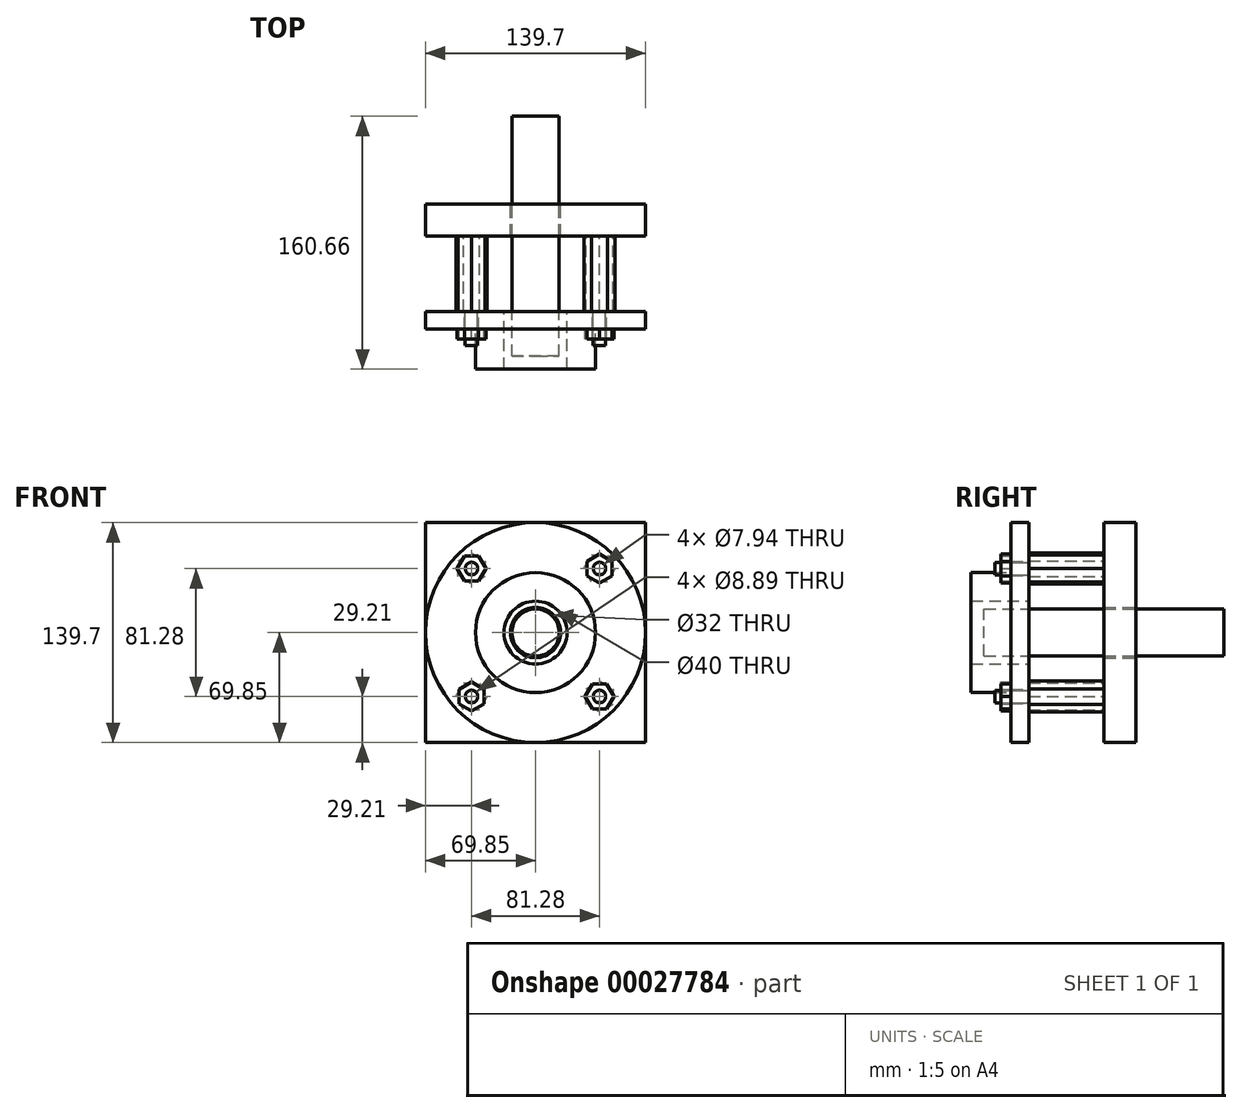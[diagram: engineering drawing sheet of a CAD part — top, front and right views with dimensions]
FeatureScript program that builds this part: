
annotation { "Feature Type Name" : "Feature", "Feature Type Description" : "" }
export const myFeature = defineFeature(function(context is Context, id is Id, definition is map)
    precondition{}
    {
        {
            var Q0;
            Q0=qCreatedBy(makeId("Front.planeOp"),FACE);
            var sketch = newSketch(context, id + "F0", { "sketchPlane" : qUnion([Q0])});
            skCircle(sketch, "E0", {"center": v(0, 0) * mm, "radius": 16 * mm});
            skLineSegment(sketch, "E1.bottom", {"start": v(-69.85, 69.85) * mm, "end": v(69.85, 69.85) * mm});
            skLineSegment(sketch, "E1.top", {"start": v(-69.85, -69.85) * mm, "end": v(69.85, -69.85) * mm});
            skLineSegment(sketch, "E1.left", {"start": v(-69.85, 69.85) * mm, "end": v(-69.85, -69.85) * mm});
            skLineSegment(sketch, "E1.right", {"start": v(69.85, 69.85) * mm, "end": v(69.85, -69.85) * mm});
            skSolve(sketch);
        }
        {
            var Q0;
            Q0=makeQuery(id+"F0.imprint","IMPRINT",FACE,{"disambiguationData":[TD([[makeQuery(id+"F0.imprint","IMPRINT",EDGE,{"derivedFrom":sQuery(id+"F0.wireOp",EDGE,"E0")}),-1.0]])]});
            extrude(context, id + "F1", {"entities" : qUnion([Q0]), "depth" : 20.32 * mm});
        }
        {
            var Q0;
            Q0=makeQuery(id+"F1.opExtrude","CAP_FACE",FACE,{"disambiguationData":[OSD([sQuery(id+"F0.wireOp",EDGE,"E0"),sQuery(id+"F0.wireOp",EDGE,"E1.bottom"),sQuery(id+"F0.wireOp",EDGE,"E1.top"),sQuery(id+"F0.wireOp",EDGE,"E1.left"),sQuery(id+"F0.wireOp",EDGE,"E1.right")])],"isStart":false});
            var sketch = newSketch(context, id + "F2", { "sketchPlane" : qUnion([Q0])});
            skLineSegment(sketch, "E2.bottom", {"start": v(-40.64, -40.64) * mm, "end": v(40.64, -40.64) * mm, "construction": true});
            skLineSegment(sketch, "E2.top", {"start": v(-40.64, 40.64) * mm, "end": v(40.64, 40.64) * mm, "construction": true});
            skLineSegment(sketch, "E2.left", {"start": v(-40.64, -40.64) * mm, "end": v(-40.64, 40.64) * mm, "construction": true});
            skLineSegment(sketch, "E2.right", {"start": v(40.64, -40.64) * mm, "end": v(40.64, 40.64) * mm, "construction": true});
            skLineSegment(sketch, "E3", {"start": v(35.7, 49.21) * mm, "end": v(45.59, 49.21) * mm});
            skLineSegment(sketch, "E4", {"start": v(45.59, 49.21) * mm, "end": v(50.54, 40.64) * mm});
            skLineSegment(sketch, "E5", {"start": v(50.54, 40.64) * mm, "end": v(45.59, 32.07) * mm});
            skLineSegment(sketch, "E6", {"start": v(45.59, 32.07) * mm, "end": v(35.7, 32.07) * mm});
            skLineSegment(sketch, "E7", {"start": v(35.7, 32.07) * mm, "end": v(30.74, 40.64) * mm});
            skLineSegment(sketch, "E8", {"start": v(30.74, 40.64) * mm, "end": v(35.7, 49.21) * mm});
            skLineSegment(sketch, "E9.1.0", {"start": v(-49.21, 35.7) * mm, "end": v(-49.21, 45.59) * mm});
            skLineSegment(sketch, "E9.1.1", {"start": v(-40.64, 30.74) * mm, "end": v(-49.21, 35.7) * mm});
            skLineSegment(sketch, "E9.1.2", {"start": v(-32.07, 35.7) * mm, "end": v(-40.64, 30.74) * mm});
            skLineSegment(sketch, "E9.1.3", {"start": v(-32.07, 45.59) * mm, "end": v(-32.07, 35.7) * mm});
            skLineSegment(sketch, "E9.1.4", {"start": v(-40.64, 50.54) * mm, "end": v(-32.07, 45.59) * mm});
            skLineSegment(sketch, "E9.1.5", {"start": v(-49.21, 45.59) * mm, "end": v(-40.64, 50.54) * mm});
            skLineSegment(sketch, "E9.2.0", {"start": v(-35.7, -49.21) * mm, "end": v(-45.59, -49.21) * mm});
            skLineSegment(sketch, "E9.2.1", {"start": v(-30.74, -40.64) * mm, "end": v(-35.7, -49.21) * mm});
            skLineSegment(sketch, "E9.2.2", {"start": v(-35.7, -32.07) * mm, "end": v(-30.74, -40.64) * mm});
            skLineSegment(sketch, "E9.2.3", {"start": v(-45.59, -32.07) * mm, "end": v(-35.7, -32.07) * mm});
            skLineSegment(sketch, "E9.2.4", {"start": v(-50.54, -40.64) * mm, "end": v(-45.59, -32.07) * mm});
            skLineSegment(sketch, "E9.2.5", {"start": v(-45.59, -49.21) * mm, "end": v(-50.54, -40.64) * mm});
            skPoint(sketch, "E9.center", {"position": v(0, 0) * mm});
            skLineSegment(sketch, "E10.1.3.0", {"start": v(49.21, -35.7) * mm, "end": v(49.21, -45.59) * mm});
            skLineSegment(sketch, "E10.3.3.0", {"start": v(40.64, -30.74) * mm, "end": v(49.21, -35.7) * mm});
            skLineSegment(sketch, "E10.6.3.0", {"start": v(32.07, -35.7) * mm, "end": v(40.64, -30.74) * mm});
            skLineSegment(sketch, "E10.9.3.0", {"start": v(32.07, -45.59) * mm, "end": v(32.07, -35.7) * mm});
            skLineSegment(sketch, "E10.12.3.0", {"start": v(40.64, -50.54) * mm, "end": v(32.07, -45.59) * mm});
            skLineSegment(sketch, "E10.15.3.0", {"start": v(49.21, -45.59) * mm, "end": v(40.64, -50.54) * mm});
            skSolve(sketch);
        }
        {
            var Q0;
            Q0=makeQuery(id+"F2.imprint","IMPRINT",FACE,{"disambiguationData":[TD([[makeQuery(id+"F2.imprint","IMPRINT",EDGE,{"derivedFrom":sQuery(id+"F2.wireOp",EDGE,"E9.1.0")}),-1.0]])]});
            var Q1;
            Q1=makeQuery(id+"F2.imprint","IMPRINT",FACE,{"disambiguationData":[TD([[makeQuery(id+"F2.imprint","IMPRINT",EDGE,{"derivedFrom":sQuery(id+"F2.wireOp",EDGE,"E3")}),-1.0]])]});
            var Q2;
            Q2=makeQuery(id+"F2.imprint","IMPRINT",FACE,{"disambiguationData":[TD([[makeQuery(id+"F2.imprint","IMPRINT",EDGE,{"derivedFrom":sQuery(id+"F2.wireOp",EDGE,"E9.3.0")}),-1.0]])]});
            var Q3;
            Q3=makeQuery(id+"F2.imprint","IMPRINT",FACE,{"disambiguationData":[TD([[makeQuery(id+"F2.imprint","IMPRINT",EDGE,{"derivedFrom":sQuery(id+"F2.wireOp",EDGE,"E9.2.0")}),-1.0]])]});
            var Q4;
            Q4=makeQuery(id+"F2.imprint","IMPRINT",FACE,{"disambiguationData":[TD([[makeQuery(id+"F2.imprint","IMPRINT",EDGE,{"derivedFrom":sQuery(id+"F2.wireOp",EDGE,"E10.1.3.0")}),-1.0]])]});
            extrude(context, id + "F3", {"entities" : qUnion([Q0, Q1, Q2, Q3, Q4]), "operationType" : NewBodyOperationType.ADD, "depth" : 47.88 * mm});
        }
        {
            var Q0;
            Q0=makeQuery(id+"F3.opExtrude","CAP_FACE",FACE,{"disambiguationData":[OSD([sQuery(id+"F2.wireOp",EDGE,"E9.1.0"),sQuery(id+"F2.wireOp",EDGE,"E9.1.1"),sQuery(id+"F2.wireOp",EDGE,"E9.1.2"),sQuery(id+"F2.wireOp",EDGE,"E9.1.3"),sQuery(id+"F2.wireOp",EDGE,"E9.1.4"),sQuery(id+"F2.wireOp",EDGE,"E9.1.5")])],"isStart":false});
            var sketch = newSketch(context, id + "F4", { "sketchPlane" : qUnion([Q0])});
            skLineSegment(sketch, "E11", {"start": v(-40.64, 50.54) * mm, "end": v(-40.64, 30.74) * mm, "construction": true});
            skLineSegment(sketch, "E12", {"start": v(-32.07, 45.59) * mm, "end": v(-49.21, 35.7) * mm, "construction": true});
            skCircle(sketch, "E13", {"center": v(-40.64, 40.64) * mm, "radius": 3.97 * mm});
            skCircle(sketch, "E14.1.0", {"center": v(-40.64, -40.64) * mm, "radius": 3.97 * mm});
            skCircle(sketch, "E14.2.0", {"center": v(40.64, -40.64) * mm, "radius": 3.97 * mm});
            skCircle(sketch, "E14.3.0", {"center": v(40.64, 40.64) * mm, "radius": 3.97 * mm});
            skPoint(sketch, "E14.center", {"position": v(0, 0) * mm});
            skSolve(sketch);
        }
        {
            var Q0;
            Q0=makeQuery(id+"F4.imprint","IMPRINT",FACE,{"disambiguationData":[TD([[makeQuery(id+"F4.imprint","IMPRINT",EDGE,{"derivedFrom":sQuery(id+"F4.wireOp",EDGE,"E13")}),1.0]])]});
            var Q1;
            Q1=makeQuery(id+"F4.imprint","IMPRINT",FACE,{"disambiguationData":[TD([[makeQuery(id+"F4.imprint","IMPRINT",EDGE,{"derivedFrom":sQuery(id+"F4.wireOp",EDGE,"E14.3.0")}),1.0]])]});
            var Q2;
            Q2=makeQuery(id+"F4.imprint","IMPRINT",FACE,{"disambiguationData":[TD([[makeQuery(id+"F4.imprint","IMPRINT",EDGE,{"derivedFrom":sQuery(id+"F4.wireOp",EDGE,"E14.2.0")}),1.0]])]});
            var Q3;
            Q3=makeQuery(id+"F4.imprint","IMPRINT",FACE,{"disambiguationData":[TD([[makeQuery(id+"F4.imprint","IMPRINT",EDGE,{"derivedFrom":sQuery(id+"F4.wireOp",EDGE,"E14.1.0")}),1.0]])]});
            extrude(context, id + "F5", {"entities" : qUnion([Q0, Q1, Q2, Q3]), "operationType" : NewBodyOperationType.ADD, "depth" : 21.59 * mm});
        }
        {
            var Q0;
            Q0=makeQuery(id+"F1.opExtrude","CAP_FACE",FACE,{"disambiguationData":[OSD([sQuery(id+"F0.wireOp",EDGE,"E0"),sQuery(id+"F0.wireOp",EDGE,"E1.bottom"),sQuery(id+"F0.wireOp",EDGE,"E1.top"),sQuery(id+"F0.wireOp",EDGE,"E1.left"),sQuery(id+"F0.wireOp",EDGE,"E1.right")])],"isStart":false});
            var sketch = newSketch(context, id + "F6", { "sketchPlane" : qUnion([Q0])});
            skCircle(sketch, "E15", {"center": v(0, 0) * mm, "radius": 15 * mm});
            skSolve(sketch);
        }
        {
            var Q0;
            Q0=makeQuery(id+"F6.imprint","IMPRINT",FACE,{"disambiguationData":[TD([[makeQuery(id+"F6.imprint","IMPRINT",EDGE,{"derivedFrom":sQuery(id+"F6.wireOp",EDGE,"E15")}),1.0]])]});
            extrude(context, id + "F7", {"entities" : qUnion([Q0]), "endBound" : BoundingType.SYMMETRIC, "depth" : 152.4 * mm});
        }
        {
            var Q0;
            Q0=makeQuery(id+"F3.opExtrude","CAP_FACE",FACE,{"disambiguationData":[OSD([sQuery(id+"F2.wireOp",EDGE,"E9.1.0"),sQuery(id+"F2.wireOp",EDGE,"E9.1.1"),sQuery(id+"F2.wireOp",EDGE,"E9.1.2"),sQuery(id+"F2.wireOp",EDGE,"E9.1.3"),sQuery(id+"F2.wireOp",EDGE,"E9.1.4"),sQuery(id+"F2.wireOp",EDGE,"E9.1.5")])],"isStart":false});
            var sketch = newSketch(context, id + "F8", { "sketchPlane" : qUnion([Q0])});
            skCircle(sketch, "E16", {"center": v(0, 0) * mm, "radius": 69.85 * mm});
            skCircle(sketch, "E17", {"center": v(-40.64, 40.64) * mm, "radius": 4.45 * mm});
            skCircle(sketch, "E18.1.0", {"center": v(-40.64, -40.64) * mm, "radius": 4.45 * mm});
            skCircle(sketch, "E18.2.0", {"center": v(40.64, -40.64) * mm, "radius": 4.45 * mm});
            skCircle(sketch, "E18.3.0", {"center": v(40.64, 40.64) * mm, "radius": 4.45 * mm});
            skCircle(sketch, "E19", {"center": v(0, 0) * mm, "radius": 20 * mm});
            skSolve(sketch);
        }
        {
            var Q0;
            Q0=makeQuery(id+"F8.imprint","IMPRINT",FACE,{"disambiguationData":[TD([[makeQuery(id+"F8.imprint","IMPRINT",EDGE,{"derivedFrom":sQuery(id+"F8.wireOp",EDGE,"E16")}),1.0]])]});
            var Q1;
            Q1=makeQuery(id+"F8.imprint","IMPRINT",FACE,{"disambiguationData":[TD([[makeQuery(id+"F8.imprint","IMPRINT",EDGE,{"derivedFrom":sQuery(id+"F8.wireOp",EDGE,"E17")}),-1.0]])]});
            extrude(context, id + "F9", {"entities" : qUnion([Q0, Q1]), "depth" : 11.18 * mm});
        }
        {
            var Q0;
            Q0=makeQuery(id+"F9.opExtrude","CAP_FACE",FACE,{"disambiguationData":[OSD([sQuery(id+"F8.wireOp",EDGE,"E16"),sQuery(id+"F8.wireOp",EDGE,"E17"),sQuery(id+"F8.wireOp",EDGE,"E18.1.0"),sQuery(id+"F8.wireOp",EDGE,"E18.2.0"),sQuery(id+"F8.wireOp",EDGE,"E18.3.0"),sQuery(id+"F8.wireOp",EDGE,"E19")])],"isStart":false});
            var sketch = newSketch(context, id + "F10", { "sketchPlane" : qUnion([Q0])});
            skCircle(sketch, "E20", {"center": v(0, 0) * mm, "radius": 38.1 * mm});
            skCircle(sketch, "E21", {"center": v(0, 0) * mm, "radius": 20 * mm});
            skSolve(sketch);
        }
        {
            var Q0;
            Q0=makeQuery(id+"F10.imprint","IMPRINT",FACE,{"disambiguationData":[TD([[makeQuery(id+"F10.imprint","IMPRINT",EDGE,{"derivedFrom":sQuery(id+"F10.wireOp",EDGE,"E20")}),1.0]])]});
            extrude(context, id + "F11", {"entities" : qUnion([Q0]), "operationType" : NewBodyOperationType.ADD, "depth" : 25.4 * mm});
        }
        {
            var Q0;
            Q0=makeQuery(id+"F9.opExtrude","CAP_FACE",FACE,{"disambiguationData":[OSD([sQuery(id+"F8.wireOp",EDGE,"E16"),sQuery(id+"F8.wireOp",EDGE,"E17"),sQuery(id+"F8.wireOp",EDGE,"E18.1.0"),sQuery(id+"F8.wireOp",EDGE,"E18.2.0"),sQuery(id+"F8.wireOp",EDGE,"E18.3.0"),sQuery(id+"F8.wireOp",EDGE,"E19")])],"isStart":false});
            var sketch = newSketch(context, id + "F12", { "sketchPlane" : qUnion([Q0])});
            skCircle(sketch, "E22.cCircle", {"center": v(-40.64, 40.64) * mm, "radius": 7.94 * mm, "construction": true});
            skLineSegment(sketch, "E22.0", {"start": v(-36.06, 48.58) * mm, "end": v(-31.47, 40.64) * mm});
            skLineSegment(sketch, "E22.1", {"start": v(-31.47, 40.64) * mm, "end": v(-36.06, 32.7) * mm});
            skLineSegment(sketch, "E22.2", {"start": v(-36.06, 32.7) * mm, "end": v(-45.22, 32.7) * mm});
            skLineSegment(sketch, "E22.3", {"start": v(-45.22, 32.7) * mm, "end": v(-49.8, 40.64) * mm});
            skLineSegment(sketch, "E22.4", {"start": v(-49.8, 40.64) * mm, "end": v(-45.22, 48.58) * mm});
            skLineSegment(sketch, "E22.5", {"start": v(-45.22, 48.58) * mm, "end": v(-36.06, 48.58) * mm});
            skPoint(sketch, "E22.0.midPoint", {"position": v(-33.77, 44.6) * mm});
            skCircle(sketch, "E23", {"center": v(-40.64, 40.64) * mm, "radius": 3.97 * mm});
            skSolve(sketch);
        }
        {
            var Q0;
            Q0=makeQuery(id+"F12.imprint","IMPRINT",FACE,{"disambiguationData":[TD([[makeQuery(id+"F12.imprint","IMPRINT",EDGE,{"derivedFrom":sQuery(id+"F12.wireOp",EDGE,"E22.0")}),-1.0]])]});
            var Q1;
            Q1=makeQuery(id+"F12.imprint","IMPRINT",FACE,{"disambiguationData":[TD([[makeQuery(id+"F12.imprint","IMPRINT",EDGE,{"derivedFrom":sQuery(id+"F12.wireOp",EDGE,"E23")}),-1.0]])]});
            extrude(context, id + "F13", {"entities" : qUnion([Q0, Q1]), "depth" : 6.35 * mm});
        }
        {
            var Q0;
            Q0=makeQuery(id+"F13.opExtrude","SWEPT_BODY",BODY,{"disambiguationData":[OSD([sQuery(id+"F12.wireOp",EDGE,"E22.0"),sQuery(id+"F12.wireOp",EDGE,"E22.1"),sQuery(id+"F12.wireOp",EDGE,"E22.2"),sQuery(id+"F12.wireOp",EDGE,"E22.3"),sQuery(id+"F12.wireOp",EDGE,"E22.4"),sQuery(id+"F12.wireOp",EDGE,"E22.5"),sQuery(id+"F12.wireOp",EDGE,"E23")])]});
            var Q1;
            Q1=makeQuery(id+"F11.opExtrude","CAP_EDGE",EDGE,{"disambiguationData":[OSD([sQuery(id+"F10.wireOp",EDGE,"E21")])],"isStart":false});
            circularPattern(context, id + "F14", {"entities" : qUnion([Q0]), "axis" : qUnion([Q1]), "angle" : 90 * degree, "instanceCount" : 4});
        }
    });
